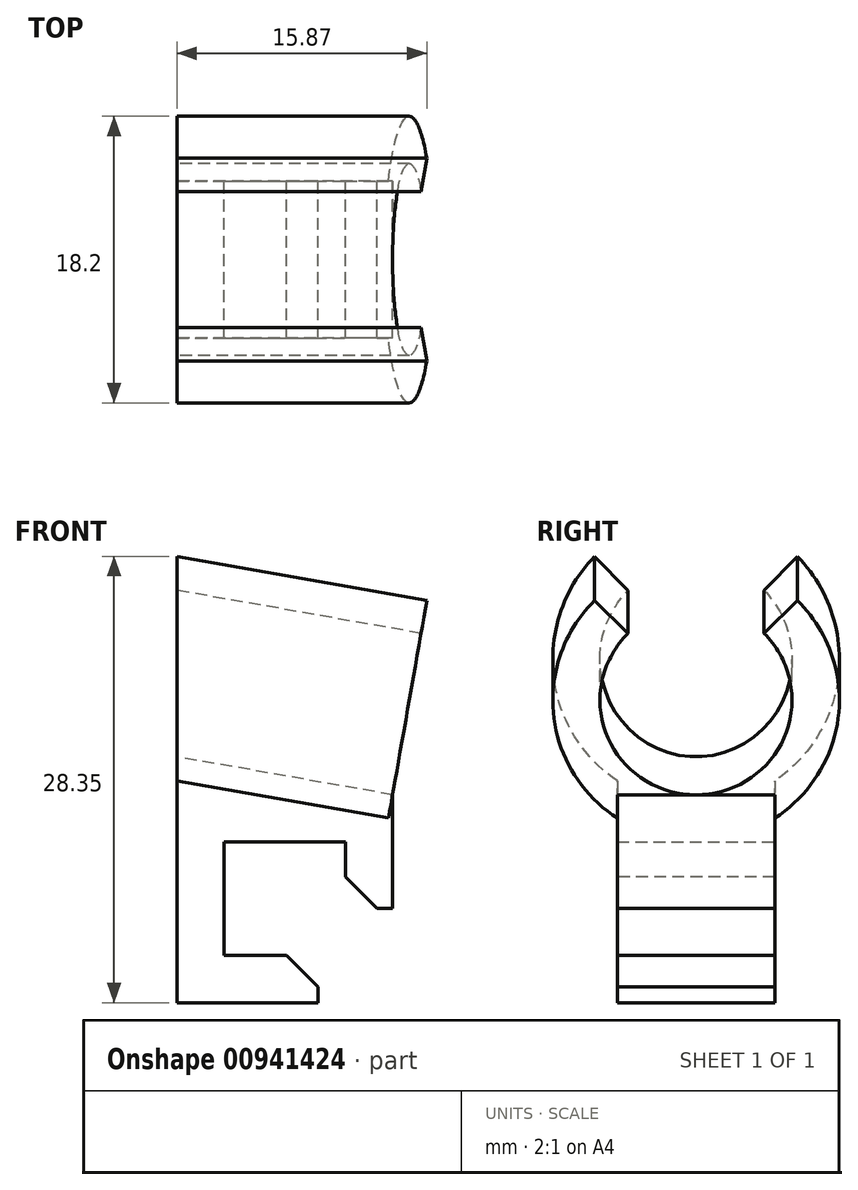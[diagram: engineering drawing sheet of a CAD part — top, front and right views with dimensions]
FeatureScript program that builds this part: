
annotation { "Feature Type Name" : "Feature", "Feature Type Description" : "" }
export const myFeature = defineFeature(function(context is Context, id is Id, definition is map)
    precondition{}
    {
        {
            var Q0;
            Q0=qCreatedBy(makeId("Top.planeOp"),FACE);
            var sketch = newSketch(context, id + "F0", { "sketchPlane" : qUnion([Q0])});
            skLineSegment(sketch, "E0", {"start": v(0, 0) * mm, "end": v(0, 28.3) * mm, "construction": true});
            skSolve(sketch);
        }
        {
            var Q0;
            Q0=sQuery(id+"F0.wireOp",EDGE,"E0");
            cPlane(context, id + "F1", {"entities" : qUnion([Q0]), "cplaneType" : CPlaneType.LINE_ANGLE, "offset" : 25 * mm, "angle" : 100 * degree, "width" : 150 * mm, "height" : 150 * mm});
        }
        {
            var Q0;
            Q0=qCreatedBy(id+"F1.planeOp",FACE);
            var sketch = newSketch(context, id + "F2", { "sketchPlane" : qUnion([Q0])});
            skCircle(sketch, "E1", {"center": v(0, 0) * mm, "radius": 6.1 * mm});
            skCircle(sketch, "E2.0", {"center": v(0, 0) * mm, "radius": 9.1 * mm});
            skLineSegment(sketch, "E3", {"start": v(0, 0) * mm, "end": v(-6.43, 6.43) * mm});
            skLineSegment(sketch, "E4.MirrorCS", {"start": v(0, 0) * mm, "end": v(6.43, 6.43) * mm});
            skSolve(sketch);
        }
        {
            var Q0;
            {var subQ0=sQuery(id+"F2.wireOp",EDGE,"E3");var subQ1=sQuery(id+"F2.wireOp",EDGE,"E1");var subQ2=makeQuery(id+"F2.imprint","INTERSECT",VERTEX,{"derivedFrom":[subQ1,subQ0]});Q0=makeQuery(id+"F2.imprint","IMPRINT",FACE,{"disambiguationData":[TD([[makeQuery(id+"F2.imprint","IMPRINT",EDGE,{"disambiguationData":[TD([[subQ2,-1.0]])],"derivedFrom":subQ1}),-1.0]])]});}
            extrude(context, id + "F3", {"entities" : qUnion([Q0]), "depth" : 14 * mm, "offsetDistance" : 25 * mm});
        }
        {
            var Q0;
            Q0=qCreatedBy(makeId("Front.planeOp"),FACE);
            var sketch = newSketch(context, id + "F4", { "sketchPlane" : qUnion([Q0])});
            skLineSegment(sketch, "E5", {"start": v(-0.97, -21.64) * mm, "end": v(7.98, -21.64) * mm});
            skLineSegment(sketch, "E6", {"start": v(2.03, -11.44) * mm, "end": v(9.73, -11.44) * mm});
            skLineSegment(sketch, "E7", {"start": v(9.73, -11.44) * mm, "end": v(9.73, -15.64) * mm});
            skLineSegment(sketch, "E8", {"start": v(9.73, -15.64) * mm, "end": v(12.73, -15.64) * mm});
            skLineSegment(sketch, "E9", {"start": v(12.73, -15.64) * mm, "end": v(12.73, -11.44) * mm});
            skLineSegment(sketch, "E10", {"start": v(2.03, -11.44) * mm, "end": v(2.03, -18.64) * mm});
            skLineSegment(sketch, "E11", {"start": v(2.03, -18.64) * mm, "end": v(7.98, -18.64) * mm});
            skLineSegment(sketch, "E12", {"start": v(7.98, -18.64) * mm, "end": v(7.98, -21.64) * mm});
            skLineSegment(sketch, "E13", {"start": v(-0.97, -8.44) * mm, "end": v(12.73, -8.44) * mm});
            skLineSegment(sketch, "E14", {"start": v(12.73, -8.44) * mm, "end": v(12.73, -11.44) * mm});
            skLineSegment(sketch, "E15", {"start": v(-0.97, -8.44) * mm, "end": v(-0.97, -21.64) * mm});
            skSolve(sketch);
        }
        {
            var Q0;
            {var subQ1=sQuery(id+"F4.wireOp",EDGE,"fSeAijJ7-2Z1f-iYIv-Fp9k-43bULN42XRhR");Q0=makeQuery(id+"F4.imprint","IMPRINT",FACE,{"disambiguationData":[TD([[makeQuery(id+"F4.imprint","IMPRINT",EDGE,{"derivedFrom":subQ1}),1.0]])]});}
            var Q1;
            {var subQ0=sQuery(id+"F4.wireOp",EDGE,"E7");Q1=makeQuery(id+"F4.imprint","IMPRINT",FACE,{"disambiguationData":[TD([[makeQuery(id+"F4.imprint","IMPRINT",EDGE,{"derivedFrom":subQ0}),1.0]])]});}
            var Q2;
            {var subQ0=sQuery(id+"F4.wireOp",EDGE,"E6");Q2=makeQuery(id+"F4.imprint","IMPRINT",FACE,{"disambiguationData":[TD([[makeQuery(id+"F4.imprint","IMPRINT",EDGE,{"derivedFrom":subQ0}),1.0]])]});}
            extrude(context, id + "F5", {"entities" : qUnion([Q0, Q1, Q2]), "operationType" : NewBodyOperationType.ADD, "endBound" : BoundingType.SYMMETRIC, "depth" : 10 * mm, "offsetDistance" : 25 * mm});
        }
        {
            var Q0;
            Q0=makeQuery(id+"F5.opExtrude","SWEPT_EDGE",EDGE,{"disambiguationData":[OSD([sQuery(id+"F4.wireOp",EDGE,"E7"),sQuery(id+"F4.wireOp",EDGE,"E8")])]});
            var Q1;
            Q1=makeQuery(id+"F5.opExtrude","SWEPT_EDGE",EDGE,{"disambiguationData":[OSD([sQuery(id+"F4.wireOp",EDGE,"E11"),sQuery(id+"F4.wireOp",EDGE,"E12")])]});
            chamfer(context, id + "F6", {"entities" : qUnion([Q0, Q1]), "width" : 2 * mm, "tangentPropagation" : true});
        }
        {
            var Q0;
            Q0=makeQuery(id+"F3.opExtrude","CAP_FACE",FACE,{"disambiguationData":[OSD([sQuery(id+"F2.wireOp",EDGE,"E1"),sQuery(id+"F2.wireOp",EDGE,"E2.0"),sQuery(id+"F2.wireOp",EDGE,"E3"),sQuery(id+"F2.wireOp",EDGE,"E4.MirrorCS")])],"isStart":true});
            extrude(context, id + "F7", {"entities" : qUnion([Q0]), "operationType" : NewBodyOperationType.ADD, "depth" : 25 * mm, "offsetDistance" : 25 * mm});
        }
        {
            var Q0;
            Q0=makeQuery(id+"F5.opExtrude","SWEPT_FACE",FACE,{"disambiguationData":[OSD([sQuery(id+"F4.wireOp",EDGE,"E15")])]});
            var sketch = newSketch(context, id + "F8", { "sketchPlane" : qUnion([Q0])});
            skLineSegment(sketch, "E16.bottom", {"start": v(22.69, 11.55) * mm, "end": v(-22.69, 11.55) * mm});
            skLineSegment(sketch, "E16.top", {"start": v(22.69, -11.55) * mm, "end": v(-22.69, -11.55) * mm});
            skLineSegment(sketch, "E16.left", {"start": v(22.69, 11.55) * mm, "end": v(22.69, -11.55) * mm});
            skLineSegment(sketch, "E16.right", {"start": v(-22.69, 11.55) * mm, "end": v(-22.69, -11.55) * mm});
            skPoint(sketch, "E16.middle", {"position": v(0, 0) * mm});
            skSolve(sketch);
        }
        {
            var Q0;
            Q0=makeQuery(id+"F8.imprint","IMPRINT",FACE,{"disambiguationData":[TD([[makeQuery(id+"F8.imprint","IMPRINT",EDGE,{"derivedFrom":sQuery(id+"F8.wireOp",EDGE,"E16.bottom")}),1.0]])]});
            extrude(context, id + "F9", {"entities" : qUnion([Q0]), "operationType" : NewBodyOperationType.REMOVE, "depth" : 51.6 * mm, "offsetDistance" : 25 * mm});
        }
        {
            var Q0;
            {var subQ0=sQuery(id+"F4.wireOp",EDGE,"E15");var subQ1=sQuery(id+"F4.wireOp",EDGE,"E13");Q0=makeQuery(id+"F5.boolean.opBoolean","SPLIT",FACE,{"disambiguationData":[TD([makeQuery(id+"F5.opExtrude","CAP_FACE",FACE,{"disambiguationData":[OSD([sQuery(id+"F4.wireOp",EDGE,"E5"),sQuery(id+"F4.wireOp",EDGE,"E6"),sQuery(id+"F4.wireOp",EDGE,"E7"),sQuery(id+"F4.wireOp",EDGE,"E8"),sQuery(id+"F4.wireOp",EDGE,"E9"),sQuery(id+"F4.wireOp",EDGE,"E10"),sQuery(id+"F4.wireOp",EDGE,"E11"),sQuery(id+"F4.wireOp",EDGE,"E12"),subQ1,sQuery(id+"F4.wireOp",EDGE,"E14"),subQ0])],"isStart":false})])],"derivedFrom":makeQuery(id+"F5.opExtrude","SWEPT_FACE",FACE,{"disambiguationData":[OSD([subQ1])]})});}
            var Q1;
            {var subQ0=sQuery(id+"F4.wireOp",EDGE,"E15");var subQ1=sQuery(id+"F4.wireOp",EDGE,"E13");Q1=makeQuery(id+"F5.boolean.opBoolean","SPLIT",FACE,{"disambiguationData":[TD([makeQuery(id+"F5.opExtrude","CAP_FACE",FACE,{"disambiguationData":[OSD([sQuery(id+"F4.wireOp",EDGE,"E5"),sQuery(id+"F4.wireOp",EDGE,"E6"),sQuery(id+"F4.wireOp",EDGE,"E7"),sQuery(id+"F4.wireOp",EDGE,"E8"),sQuery(id+"F4.wireOp",EDGE,"E9"),sQuery(id+"F4.wireOp",EDGE,"E10"),sQuery(id+"F4.wireOp",EDGE,"E11"),sQuery(id+"F4.wireOp",EDGE,"E12"),subQ1,sQuery(id+"F4.wireOp",EDGE,"E14"),subQ0])],"isStart":true})])],"derivedFrom":makeQuery(id+"F5.opExtrude","SWEPT_FACE",FACE,{"disambiguationData":[OSD([subQ1])]})});}
            extrude(context, id + "F10", {"entities" : qUnion([Q0, Q1]), "operationType" : NewBodyOperationType.ADD, "depth" : 1.1 * mm, "offsetDistance" : 25 * mm});
        }
    });
